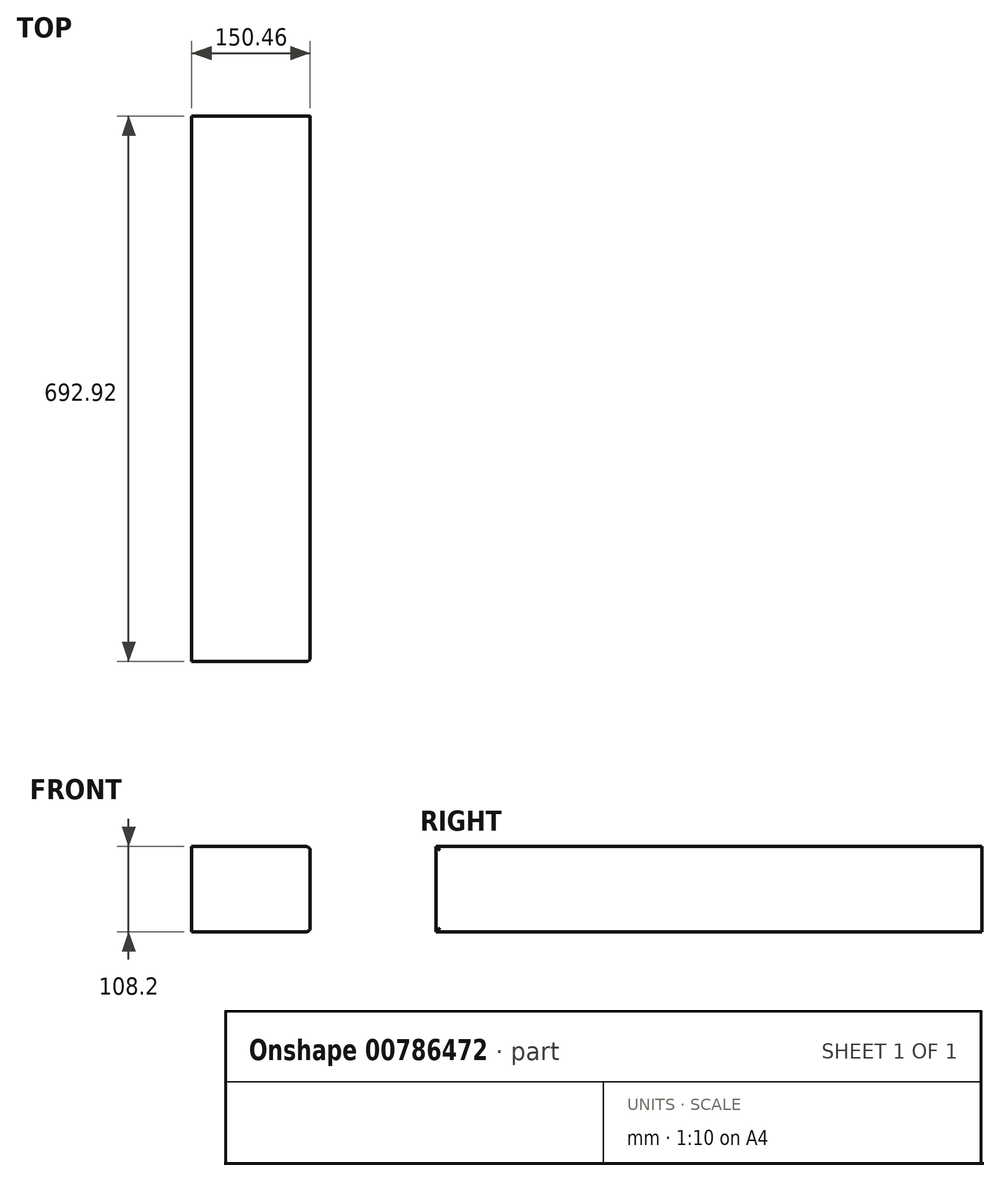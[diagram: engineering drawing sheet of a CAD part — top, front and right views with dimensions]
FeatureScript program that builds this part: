
annotation { "Feature Type Name" : "Feature", "Feature Type Description" : "" }
export const myFeature = defineFeature(function(context is Context, id is Id, definition is map)
    precondition{}
    {
        {
            var Q0;
            Q0=qCreatedBy(makeId("Front.planeOp"),FACE);
            var sketch = newSketch(context, id + "F0", { "sketchPlane" : qUnion([Q0])});
            skLineSegment(sketch, "E0.bottom", {"start": v(-37.22, -29.37) * mm, "end": v(113.24, -29.37) * mm});
            skLineSegment(sketch, "E0.top", {"start": v(-37.22, 78.83) * mm, "end": v(113.24, 78.83) * mm});
            skLineSegment(sketch, "E0.left", {"start": v(-37.22, -29.37) * mm, "end": v(-37.22, 78.83) * mm});
            skLineSegment(sketch, "E0.right", {"start": v(113.24, -29.37) * mm, "end": v(113.24, 78.83) * mm});
            skSolve(sketch);
        }
        {
            var Q0;
            Q0=makeQuery(id+"F0.imprint","IMPRINT",FACE,{"disambiguationData":[TD([[makeQuery(id+"F0.imprint","IMPRINT",EDGE,{"derivedFrom":sQuery(id+"F0.wireOp",EDGE,"E0.bottom")}),1.0]])]});
            extrude(context, id + "F1", {"entities" : qUnion([Q0]), "depth" : 692.92 * mm, "offsetDistance" : 25.4 * mm});
        }
        {
            var Q0;
            Q0=makeQuery(id+"F1.opExtrude","SWEPT_EDGE",EDGE,{"disambiguationData":[OSD([sQuery(id+"F0.wireOp",EDGE,"E0.top"),sQuery(id+"F0.wireOp",EDGE,"E0.right")])]});
            var Q1;
            Q1=makeQuery(id+"F1.opExtrude","CAP_EDGE",EDGE,{"disambiguationData":[OSD([sQuery(id+"F0.wireOp",EDGE,"E0.right")])],"isStart":false});
            var Q2;
            Q2=makeQuery(id+"F1.opExtrude","SWEPT_EDGE",EDGE,{"disambiguationData":[OSD([sQuery(id+"F0.wireOp",EDGE,"E0.bottom"),sQuery(id+"F0.wireOp",EDGE,"E0.right")])]});
            fillet(context, id + "F2", {"entities" : qUnion([Q0, Q1, Q2]), "radius" : 5.08 * mm, "tangentPropagation" : true, "allowEdgeOverflow" : false});
        }
    });
